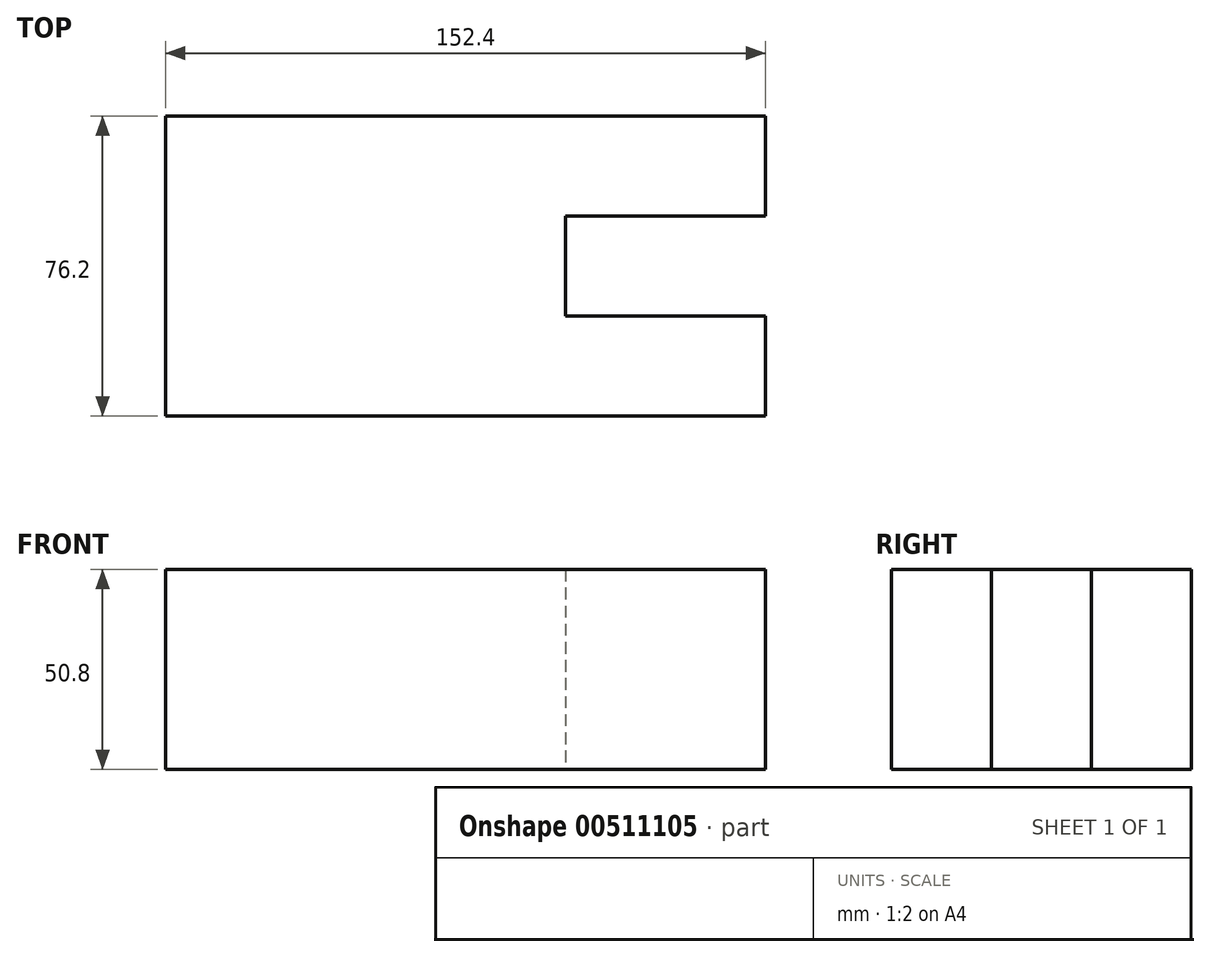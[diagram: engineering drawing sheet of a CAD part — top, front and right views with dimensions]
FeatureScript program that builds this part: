
annotation { "Feature Type Name" : "Feature", "Feature Type Description" : "" }
export const myFeature = defineFeature(function(context is Context, id is Id, definition is map)
    precondition{}
    {
        {
            var Q0;
            Q0=qCreatedBy(makeId("Top.planeOp"),FACE);
            var sketch = newSketch(context, id + "F0", { "sketchPlane" : qUnion([Q0])});
            skLineSegment(sketch, "E0", {"start": v(-70.36, 49.66) * mm, "end": v(82.04, 49.66) * mm});
            skLineSegment(sketch, "E1", {"start": v(-70.36, 49.66) * mm, "end": v(-70.36, -26.54) * mm});
            skLineSegment(sketch, "E2", {"start": v(-70.36, -26.54) * mm, "end": v(82.04, -26.54) * mm});
            skLineSegment(sketch, "E3", {"start": v(82.04, 49.66) * mm, "end": v(82.04, 24.26) * mm});
            skLineSegment(sketch, "E4", {"start": v(82.04, -26.54) * mm, "end": v(82.04, -1.14) * mm});
            skLineSegment(sketch, "E5", {"start": v(82.04, -1.14) * mm, "end": v(31.24, -1.14) * mm});
            skLineSegment(sketch, "E6", {"start": v(31.24, -1.14) * mm, "end": v(31.24, 24.26) * mm});
            skLineSegment(sketch, "E7", {"start": v(31.24, 24.26) * mm, "end": v(82.04, 24.26) * mm});
            skSolve(sketch);
        }
        {
            var Q0;
            Q0 = qSketchRegion(id + "F0", true);
            extrude(context, id + "F1", {"entities" : qUnion([Q0]), "depth" : 50.8 * mm});
        }
    });
